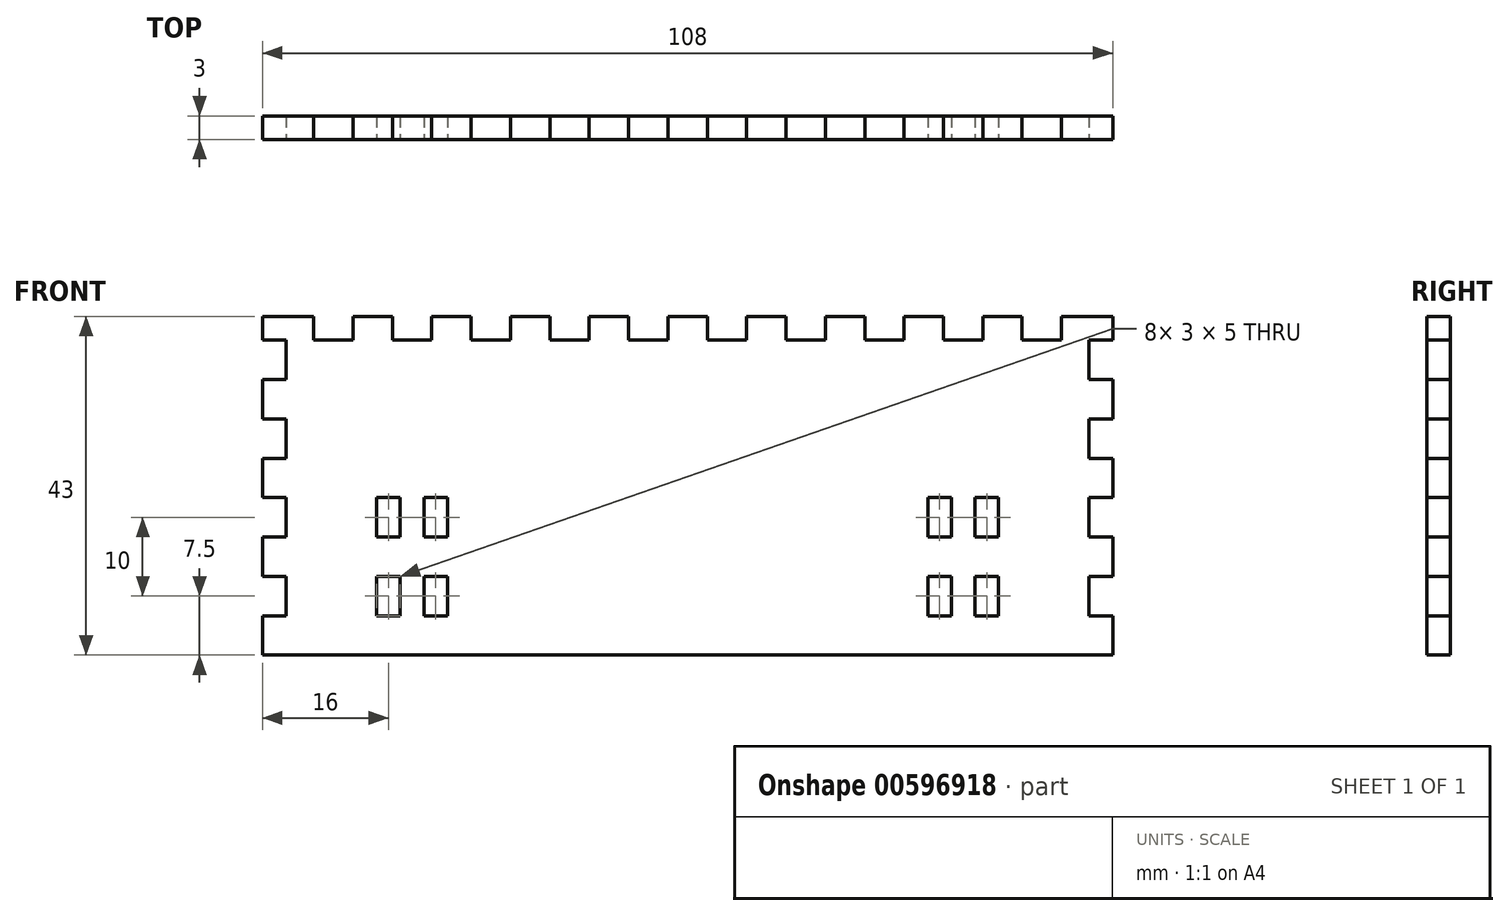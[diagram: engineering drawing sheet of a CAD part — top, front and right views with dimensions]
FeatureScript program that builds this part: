
annotation { "Feature Type Name" : "Feature", "Feature Type Description" : "" }
export const myFeature = defineFeature(function(context is Context, id is Id, definition is map)
    precondition{}
    {
        {
            var Q0;
            Q0=qCreatedBy(makeId("Front.planeOp"),FACE);
            var sketch = newSketch(context, id + "F0", { "sketchPlane" : qUnion([Q0])});
            skLineSegment(sketch, "E0.bottom", {"start": v(51, 20) * mm, "end": v(-51, 20) * mm});
            skLineSegment(sketch, "E0.top", {"start": v(51, -20) * mm, "end": v(-51, -20) * mm});
            skLineSegment(sketch, "E0.left", {"start": v(51, 20) * mm, "end": v(51, -20) * mm});
            skLineSegment(sketch, "E0.right", {"start": v(-51, 20) * mm, "end": v(-51, -20) * mm});
            skPoint(sketch, "E0.middle", {"position": v(0, 0) * mm});
            skSolve(sketch);
        }
        {
            var Q0;
            Q0=qSketchRegion(id+"F0",true);
            extrude(context, id + "F1", {"entities" : qUnion([Q0]), "depth" : 3 * mm, "offsetDistance" : 25 * mm});
        }
        {
            var Q0;
            Q0=makeQuery(id+"F1.opExtrude","CAP_FACE",FACE,{"disambiguationData":[OSD([sQuery(id+"F0.wireOp",EDGE,"E0.bottom"),sQuery(id+"F0.wireOp",EDGE,"E0.top"),sQuery(id+"F0.wireOp",EDGE,"E0.left"),sQuery(id+"F0.wireOp",EDGE,"E0.right")])],"isStart":false});
            var sketch = newSketch(context, id + "F2", { "sketchPlane" : qUnion([Q0])});
            skLineSegment(sketch, "E1.bottom", {"start": v(-51, -20) * mm, "end": v(-54, -20) * mm});
            skLineSegment(sketch, "E1.top", {"start": v(-51, -15) * mm, "end": v(-54, -15) * mm});
            skLineSegment(sketch, "E1.left", {"start": v(-51, -20) * mm, "end": v(-51, -15) * mm});
            skLineSegment(sketch, "E1.right", {"start": v(-54, -20) * mm, "end": v(-54, -15) * mm});
            skLineSegment(sketch, "E2.0.1.0", {"start": v(-51, -5) * mm, "end": v(-54, -5) * mm});
            skLineSegment(sketch, "E2.0.1.1", {"start": v(-54, -10) * mm, "end": v(-54, -5) * mm});
            skLineSegment(sketch, "E2.0.1.2", {"start": v(-51, -10) * mm, "end": v(-51, -5) * mm});
            skLineSegment(sketch, "E2.0.1.3", {"start": v(-51, -10) * mm, "end": v(-54, -10) * mm});
            skLineSegment(sketch, "E2.0.2.0", {"start": v(-51, 5) * mm, "end": v(-54, 5) * mm});
            skLineSegment(sketch, "E2.0.2.1", {"start": v(-54, 0) * mm, "end": v(-54, 5) * mm});
            skLineSegment(sketch, "E2.0.2.2", {"start": v(-51, 0) * mm, "end": v(-51, 5) * mm});
            skLineSegment(sketch, "E2.0.2.3", {"start": v(-51, 0) * mm, "end": v(-54, 0) * mm});
            skLineSegment(sketch, "E2.0.3.0", {"start": v(-51, 15) * mm, "end": v(-54, 15) * mm});
            skLineSegment(sketch, "E2.0.3.1", {"start": v(-54, 10) * mm, "end": v(-54, 15) * mm});
            skLineSegment(sketch, "E2.0.3.2", {"start": v(-51, 10) * mm, "end": v(-51, 15) * mm});
            skLineSegment(sketch, "E2.0.3.3", {"start": v(-51, 10) * mm, "end": v(-54, 10) * mm});
            skLineSegment(sketch, "E2.direction1", {"start": v(-54, -15) * mm, "end": v(-29, -15) * mm, "construction": true});
            skLineSegment(sketch, "E2.direction2", {"start": v(-54, -15) * mm, "end": v(-54, -5) * mm, "construction": true});
            skLineSegment(sketch, "E3.MirrorCS", {"start": v(54, -10) * mm, "end": v(54, -5) * mm});
            skLineSegment(sketch, "E4.MirrorCS", {"start": v(51, -5) * mm, "end": v(54, -5) * mm});
            skLineSegment(sketch, "E5.MirrorCS", {"start": v(51, -20) * mm, "end": v(51, -15) * mm});
            skLineSegment(sketch, "E6.MirrorCS", {"start": v(54, 10) * mm, "end": v(54, 15) * mm});
            skLineSegment(sketch, "E7.MirrorCS", {"start": v(51, -20) * mm, "end": v(54, -20) * mm});
            skLineSegment(sketch, "E8.MirrorCS", {"start": v(51, -15) * mm, "end": v(54, -15) * mm});
            skLineSegment(sketch, "E9.MirrorCS", {"start": v(54, -20) * mm, "end": v(54, -15) * mm});
            skLineSegment(sketch, "E10.MirrorCS", {"start": v(51, 15) * mm, "end": v(54, 15) * mm});
            skLineSegment(sketch, "E11.MirrorCS", {"start": v(51, 10) * mm, "end": v(54, 10) * mm});
            skLineSegment(sketch, "E12.MirrorCS", {"start": v(54, -15) * mm, "end": v(54, -5) * mm, "construction": true});
            skLineSegment(sketch, "E13.MirrorCS", {"start": v(51, 10) * mm, "end": v(51, 15) * mm});
            skLineSegment(sketch, "E14.MirrorCS", {"start": v(54, 0) * mm, "end": v(54, 5) * mm});
            skLineSegment(sketch, "E15.MirrorCS", {"start": v(51, 0) * mm, "end": v(51, 5) * mm});
            skLineSegment(sketch, "E16.MirrorCS", {"start": v(51, 0) * mm, "end": v(54, 0) * mm});
            skLineSegment(sketch, "E17.MirrorCS", {"start": v(51, -10) * mm, "end": v(51, -5) * mm});
            skLineSegment(sketch, "E18.MirrorCS", {"start": v(51, -10) * mm, "end": v(54, -10) * mm});
            skLineSegment(sketch, "E19.MirrorCS", {"start": v(51, 5) * mm, "end": v(54, 5) * mm});
            skSolve(sketch);
        }
        {
            var Q0;
            Q0=qSketchRegion(id+"F2",true);
            extrude(context, id + "F3", {"entities" : qUnion([Q0]), "operationType" : NewBodyOperationType.ADD, "oppositeDirection" : true, "depth" : 3 * mm, "offsetDistance" : 25 * mm});
        }
        {
            var Q0;
            Q0=makeQuery(id+"F3.boolean.opBoolean","MERGE",FACE,{"derivedFrom":[makeQuery(id+"F1.opExtrude","CAP_FACE",FACE,{"disambiguationData":[OSD([sQuery(id+"F0.wireOp",EDGE,"E0.bottom"),sQuery(id+"F0.wireOp",EDGE,"E0.top"),sQuery(id+"F0.wireOp",EDGE,"E0.left"),sQuery(id+"F0.wireOp",EDGE,"E0.right")])],"isStart":true}),makeQuery(id+"F3.opExtrude","CAP_FACE",FACE,{"disambiguationData":[OSD([sQuery(id+"F2.wireOp",EDGE,"E1.bottom"),sQuery(id+"F2.wireOp",EDGE,"E1.top"),sQuery(id+"F2.wireOp",EDGE,"E1.left"),sQuery(id+"F2.wireOp",EDGE,"E1.right")])],"isStart":false}),makeQuery(id+"F3.opExtrude","CAP_FACE",FACE,{"disambiguationData":[OSD([sQuery(id+"F2.wireOp",EDGE,"E2.0.1.0"),sQuery(id+"F2.wireOp",EDGE,"E2.0.1.1"),sQuery(id+"F2.wireOp",EDGE,"E2.0.1.2"),sQuery(id+"F2.wireOp",EDGE,"E2.0.1.3")])],"isStart":false}),makeQuery(id+"F3.opExtrude","CAP_FACE",FACE,{"disambiguationData":[OSD([sQuery(id+"F2.wireOp",EDGE,"E2.0.2.0"),sQuery(id+"F2.wireOp",EDGE,"E2.0.2.1"),sQuery(id+"F2.wireOp",EDGE,"E2.0.2.2"),sQuery(id+"F2.wireOp",EDGE,"E2.0.2.3")])],"isStart":false}),makeQuery(id+"F3.opExtrude","CAP_FACE",FACE,{"disambiguationData":[OSD([sQuery(id+"F2.wireOp",EDGE,"E2.0.3.0"),sQuery(id+"F2.wireOp",EDGE,"E2.0.3.1"),sQuery(id+"F2.wireOp",EDGE,"E2.0.3.2"),sQuery(id+"F2.wireOp",EDGE,"E2.0.3.3")])],"isStart":false}),makeQuery(id+"F3.opExtrude","CAP_FACE",FACE,{"disambiguationData":[OSD([sQuery(id+"F2.wireOp",EDGE,"E3.MirrorCS"),sQuery(id+"F2.wireOp",EDGE,"E4.MirrorCS"),sQuery(id+"F2.wireOp",EDGE,"E17.MirrorCS"),sQuery(id+"F2.wireOp",EDGE,"E18.MirrorCS")])],"isStart":false}),makeQuery(id+"F3.opExtrude","CAP_FACE",FACE,{"disambiguationData":[OSD([sQuery(id+"F2.wireOp",EDGE,"E5.MirrorCS"),sQuery(id+"F2.wireOp",EDGE,"E7.MirrorCS"),sQuery(id+"F2.wireOp",EDGE,"E8.MirrorCS"),sQuery(id+"F2.wireOp",EDGE,"E9.MirrorCS")])],"isStart":false}),makeQuery(id+"F3.opExtrude","CAP_FACE",FACE,{"disambiguationData":[OSD([sQuery(id+"F2.wireOp",EDGE,"E6.MirrorCS"),sQuery(id+"F2.wireOp",EDGE,"E10.MirrorCS"),sQuery(id+"F2.wireOp",EDGE,"E11.MirrorCS"),sQuery(id+"F2.wireOp",EDGE,"E13.MirrorCS")])],"isStart":false}),makeQuery(id+"F3.opExtrude","CAP_FACE",FACE,{"disambiguationData":[OSD([sQuery(id+"F2.wireOp",EDGE,"E14.MirrorCS"),sQuery(id+"F2.wireOp",EDGE,"E15.MirrorCS"),sQuery(id+"F2.wireOp",EDGE,"E16.MirrorCS"),sQuery(id+"F2.wireOp",EDGE,"E19.MirrorCS")])],"isStart":false})]});
            var sketch = newSketch(context, id + "F4", { "sketchPlane" : qUnion([Q0])});
            skLineSegment(sketch, "E20", {"start": v(0, 20) * mm, "end": v(0, 21.5) * mm, "construction": true});
            skLineSegment(sketch, "E21.bottom", {"start": v(-2.5, 20) * mm, "end": v(2.5, 20) * mm});
            skLineSegment(sketch, "E21.top", {"start": v(-2.5, 23) * mm, "end": v(2.5, 23) * mm});
            skLineSegment(sketch, "E21.left", {"start": v(-2.5, 20) * mm, "end": v(-2.5, 23) * mm});
            skLineSegment(sketch, "E21.right", {"start": v(2.5, 20) * mm, "end": v(2.5, 23) * mm});
            skPoint(sketch, "E21.middle", {"position": v(0, 21.5) * mm});
            skLineSegment(sketch, "E22.1.0.0", {"start": v(7.5, 23) * mm, "end": v(12.5, 23) * mm});
            skLineSegment(sketch, "E22.1.0.1", {"start": v(12.5, 20) * mm, "end": v(12.5, 23) * mm});
            skLineSegment(sketch, "E22.1.0.2", {"start": v(7.5, 20) * mm, "end": v(12.5, 20) * mm});
            skLineSegment(sketch, "E22.1.0.3", {"start": v(7.5, 20) * mm, "end": v(7.5, 23) * mm});
            skLineSegment(sketch, "E22.2.0.0", {"start": v(17.5, 23) * mm, "end": v(22.5, 23) * mm});
            skLineSegment(sketch, "E22.2.0.1", {"start": v(22.5, 20) * mm, "end": v(22.5, 23) * mm});
            skLineSegment(sketch, "E22.2.0.2", {"start": v(17.5, 20) * mm, "end": v(22.5, 20) * mm});
            skLineSegment(sketch, "E22.2.0.3", {"start": v(17.5, 20) * mm, "end": v(17.5, 23) * mm});
            skLineSegment(sketch, "E22.3.0.0", {"start": v(27.5, 23) * mm, "end": v(32.5, 23) * mm});
            skLineSegment(sketch, "E22.3.0.1", {"start": v(32.5, 20) * mm, "end": v(32.5, 23) * mm});
            skLineSegment(sketch, "E22.3.0.2", {"start": v(27.5, 20) * mm, "end": v(32.5, 20) * mm});
            skLineSegment(sketch, "E22.3.0.3", {"start": v(27.5, 20) * mm, "end": v(27.5, 23) * mm});
            skLineSegment(sketch, "E22.4.0.0", {"start": v(37.5, 23) * mm, "end": v(42.5, 23) * mm});
            skLineSegment(sketch, "E22.4.0.1", {"start": v(42.5, 20) * mm, "end": v(42.5, 23) * mm});
            skLineSegment(sketch, "E22.4.0.2", {"start": v(37.5, 20) * mm, "end": v(42.5, 20) * mm});
            skLineSegment(sketch, "E22.4.0.3", {"start": v(37.5, 20) * mm, "end": v(37.5, 23) * mm});
            skLineSegment(sketch, "E22.5.0.0", {"start": v(47.5, 23) * mm, "end": v(52.5, 23) * mm});
            skLineSegment(sketch, "E22.5.0.2", {"start": v(47.5, 20) * mm, "end": v(52.5, 20) * mm});
            skLineSegment(sketch, "E22.5.0.3", {"start": v(47.5, 20) * mm, "end": v(47.5, 23) * mm});
            skLineSegment(sketch, "E22.direction1", {"start": v(-2.5, 23) * mm, "end": v(7.5, 23) * mm, "construction": true});
            skLineSegment(sketch, "E23.MirrorCS", {"start": v(-47.5, 20) * mm, "end": v(-47.5, 23) * mm});
            skLineSegment(sketch, "E24.MirrorCS", {"start": v(-17.5, 20) * mm, "end": v(-17.5, 23) * mm});
            skLineSegment(sketch, "E25.MirrorCS", {"start": v(-22.5, 20) * mm, "end": v(-22.5, 23) * mm});
            skLineSegment(sketch, "E26.MirrorCS", {"start": v(-7.5, 20) * mm, "end": v(-7.5, 23) * mm});
            skLineSegment(sketch, "E27.MirrorCS", {"start": v(-12.5, 20) * mm, "end": v(-12.5, 23) * mm});
            skLineSegment(sketch, "E28.MirrorCS", {"start": v(-32.5, 20) * mm, "end": v(-32.5, 23) * mm});
            skLineSegment(sketch, "E29.MirrorCS", {"start": v(-37.5, 20) * mm, "end": v(-37.5, 23) * mm});
            skLineSegment(sketch, "E30.MirrorCS", {"start": v(-27.5, 20) * mm, "end": v(-27.5, 23) * mm});
            skLineSegment(sketch, "E31.MirrorCS", {"start": v(-42.5, 20) * mm, "end": v(-42.5, 23) * mm});
            skLineSegment(sketch, "E32.MirrorCS", {"start": v(-37.5, 23) * mm, "end": v(-42.5, 23) * mm});
            skLineSegment(sketch, "E33.MirrorCS", {"start": v(-47.5, 23) * mm, "end": v(-52.5, 23) * mm});
            skLineSegment(sketch, "E34.MirrorCS", {"start": v(-17.5, 20) * mm, "end": v(-22.5, 20) * mm});
            skLineSegment(sketch, "E35.MirrorCS", {"start": v(-17.5, 23) * mm, "end": v(-22.5, 23) * mm});
            skLineSegment(sketch, "E36.MirrorCS", {"start": v(-7.5, 20) * mm, "end": v(-12.5, 20) * mm});
            skLineSegment(sketch, "E37.MirrorCS", {"start": v(-7.5, 23) * mm, "end": v(-12.5, 23) * mm});
            skLineSegment(sketch, "E38.MirrorCS", {"start": v(-47.5, 20) * mm, "end": v(-52.5, 20) * mm});
            skLineSegment(sketch, "E39.MirrorCS", {"start": v(-27.5, 20) * mm, "end": v(-32.5, 20) * mm});
            skLineSegment(sketch, "E40.MirrorCS", {"start": v(-27.5, 23) * mm, "end": v(-32.5, 23) * mm});
            skLineSegment(sketch, "E41.MirrorCS", {"start": v(-37.5, 20) * mm, "end": v(-42.5, 20) * mm});
            skLineSegment(sketch, "E42", {"start": v(-52.5, 20) * mm, "end": v(-54, 20) * mm});
            skLineSegment(sketch, "E43", {"start": v(-54, 20) * mm, "end": v(-54, 23) * mm});
            skLineSegment(sketch, "E44", {"start": v(-54, 23) * mm, "end": v(-52.5, 23) * mm});
            skLineSegment(sketch, "E45.bottom", {"start": v(52.5, 23) * mm, "end": v(54, 23) * mm});
            skLineSegment(sketch, "E45.top", {"start": v(52.5, 20) * mm, "end": v(54, 20) * mm});
            skLineSegment(sketch, "E45.right", {"start": v(54, 23) * mm, "end": v(54, 20) * mm});
            skSolve(sketch);
        }
        {
            var Q0;
            Q0 = qSketchRegion(id + "F4", true);
            extrude(context, id + "F5", {"entities" : qUnion([Q0]), "operationType" : NewBodyOperationType.ADD, "oppositeDirection" : true, "depth" : 3 * mm, "offsetDistance" : 25 * mm});
        }
        {
            var Q0;
            Q0=makeQuery(id+"F5.boolean.opBoolean","MERGE",FACE,{"derivedFrom":[makeQuery(id+"F3.boolean.opBoolean","MERGE",FACE,{"derivedFrom":[makeQuery(id+"F1.opExtrude","CAP_FACE",FACE,{"disambiguationData":[OSD([sQuery(id+"F0.wireOp",EDGE,"E0.bottom"),sQuery(id+"F0.wireOp",EDGE,"E0.top"),sQuery(id+"F0.wireOp",EDGE,"E0.left"),sQuery(id+"F0.wireOp",EDGE,"E0.right")])],"isStart":false}),makeQuery(id+"F3.opExtrude","CAP_FACE",FACE,{"disambiguationData":[OSD([sQuery(id+"F2.wireOp",EDGE,"E1.bottom"),sQuery(id+"F2.wireOp",EDGE,"E1.top"),sQuery(id+"F2.wireOp",EDGE,"E1.left"),sQuery(id+"F2.wireOp",EDGE,"E1.right")])],"isStart":true}),makeQuery(id+"F3.opExtrude","CAP_FACE",FACE,{"disambiguationData":[OSD([sQuery(id+"F2.wireOp",EDGE,"E2.0.1.0"),sQuery(id+"F2.wireOp",EDGE,"E2.0.1.1"),sQuery(id+"F2.wireOp",EDGE,"E2.0.1.2"),sQuery(id+"F2.wireOp",EDGE,"E2.0.1.3")])],"isStart":true}),makeQuery(id+"F3.opExtrude","CAP_FACE",FACE,{"disambiguationData":[OSD([sQuery(id+"F2.wireOp",EDGE,"E2.0.2.0"),sQuery(id+"F2.wireOp",EDGE,"E2.0.2.1"),sQuery(id+"F2.wireOp",EDGE,"E2.0.2.2"),sQuery(id+"F2.wireOp",EDGE,"E2.0.2.3")])],"isStart":true}),makeQuery(id+"F3.opExtrude","CAP_FACE",FACE,{"disambiguationData":[OSD([sQuery(id+"F2.wireOp",EDGE,"E2.0.3.0"),sQuery(id+"F2.wireOp",EDGE,"E2.0.3.1"),sQuery(id+"F2.wireOp",EDGE,"E2.0.3.2"),sQuery(id+"F2.wireOp",EDGE,"E2.0.3.3")])],"isStart":true}),makeQuery(id+"F3.opExtrude","CAP_FACE",FACE,{"disambiguationData":[OSD([sQuery(id+"F2.wireOp",EDGE,"E3.MirrorCS"),sQuery(id+"F2.wireOp",EDGE,"E4.MirrorCS"),sQuery(id+"F2.wireOp",EDGE,"E17.MirrorCS"),sQuery(id+"F2.wireOp",EDGE,"E18.MirrorCS")])],"isStart":true}),makeQuery(id+"F3.opExtrude","CAP_FACE",FACE,{"disambiguationData":[OSD([sQuery(id+"F2.wireOp",EDGE,"E5.MirrorCS"),sQuery(id+"F2.wireOp",EDGE,"E7.MirrorCS"),sQuery(id+"F2.wireOp",EDGE,"E8.MirrorCS"),sQuery(id+"F2.wireOp",EDGE,"E9.MirrorCS")])],"isStart":true}),makeQuery(id+"F3.opExtrude","CAP_FACE",FACE,{"disambiguationData":[OSD([sQuery(id+"F2.wireOp",EDGE,"E6.MirrorCS"),sQuery(id+"F2.wireOp",EDGE,"E10.MirrorCS"),sQuery(id+"F2.wireOp",EDGE,"E11.MirrorCS"),sQuery(id+"F2.wireOp",EDGE,"E13.MirrorCS")])],"isStart":true}),makeQuery(id+"F3.opExtrude","CAP_FACE",FACE,{"disambiguationData":[OSD([sQuery(id+"F2.wireOp",EDGE,"E14.MirrorCS"),sQuery(id+"F2.wireOp",EDGE,"E15.MirrorCS"),sQuery(id+"F2.wireOp",EDGE,"E16.MirrorCS"),sQuery(id+"F2.wireOp",EDGE,"E19.MirrorCS")])],"isStart":true})]}),makeQuery(id+"F5.opExtrude","CAP_FACE",FACE,{"disambiguationData":[OSD([sQuery(id+"F4.wireOp",EDGE,"E21.bottom"),sQuery(id+"F4.wireOp",EDGE,"E21.top"),sQuery(id+"F4.wireOp",EDGE,"E21.left"),sQuery(id+"F4.wireOp",EDGE,"E21.right")])],"isStart":false}),makeQuery(id+"F5.opExtrude","CAP_FACE",FACE,{"disambiguationData":[OSD([sQuery(id+"F4.wireOp",EDGE,"E22.1.0.0"),sQuery(id+"F4.wireOp",EDGE,"E22.1.0.1"),sQuery(id+"F4.wireOp",EDGE,"E22.1.0.2"),sQuery(id+"F4.wireOp",EDGE,"E22.1.0.3")])],"isStart":false}),makeQuery(id+"F5.opExtrude","CAP_FACE",FACE,{"disambiguationData":[OSD([sQuery(id+"F4.wireOp",EDGE,"E22.2.0.0"),sQuery(id+"F4.wireOp",EDGE,"E22.2.0.1"),sQuery(id+"F4.wireOp",EDGE,"E22.2.0.2"),sQuery(id+"F4.wireOp",EDGE,"E22.2.0.3")])],"isStart":false}),makeQuery(id+"F5.opExtrude","CAP_FACE",FACE,{"disambiguationData":[OSD([sQuery(id+"F4.wireOp",EDGE,"E22.3.0.0"),sQuery(id+"F4.wireOp",EDGE,"E22.3.0.1"),sQuery(id+"F4.wireOp",EDGE,"E22.3.0.2"),sQuery(id+"F4.wireOp",EDGE,"E22.3.0.3")])],"isStart":false}),makeQuery(id+"F5.opExtrude","CAP_FACE",FACE,{"disambiguationData":[OSD([sQuery(id+"F4.wireOp",EDGE,"E22.4.0.0"),sQuery(id+"F4.wireOp",EDGE,"E22.4.0.1"),sQuery(id+"F4.wireOp",EDGE,"E22.4.0.2"),sQuery(id+"F4.wireOp",EDGE,"E22.4.0.3")])],"isStart":false}),makeQuery(id+"F5.opExtrude","CAP_FACE",FACE,{"disambiguationData":[OSD([sQuery(id+"F4.wireOp",EDGE,"E22.5.0.0"),sQuery(id+"F4.wireOp",EDGE,"E22.5.0.2"),sQuery(id+"F4.wireOp",EDGE,"E22.5.0.3"),sQuery(id+"F4.wireOp",EDGE,"E45.bottom"),sQuery(id+"F4.wireOp",EDGE,"E45.top"),sQuery(id+"F4.wireOp",EDGE,"E45.right")])],"isStart":false}),makeQuery(id+"F5.opExtrude","CAP_FACE",FACE,{"disambiguationData":[OSD([sQuery(id+"F4.wireOp",EDGE,"E23.MirrorCS"),sQuery(id+"F4.wireOp",EDGE,"E33.MirrorCS"),sQuery(id+"F4.wireOp",EDGE,"E38.MirrorCS"),sQuery(id+"F4.wireOp",EDGE,"E42"),sQuery(id+"F4.wireOp",EDGE,"E43"),sQuery(id+"F4.wireOp",EDGE,"E44")])],"isStart":false}),makeQuery(id+"F5.opExtrude","CAP_FACE",FACE,{"disambiguationData":[OSD([sQuery(id+"F4.wireOp",EDGE,"E24.MirrorCS"),sQuery(id+"F4.wireOp",EDGE,"E25.MirrorCS"),sQuery(id+"F4.wireOp",EDGE,"E34.MirrorCS"),sQuery(id+"F4.wireOp",EDGE,"E35.MirrorCS")])],"isStart":false}),makeQuery(id+"F5.opExtrude","CAP_FACE",FACE,{"disambiguationData":[OSD([sQuery(id+"F4.wireOp",EDGE,"E26.MirrorCS"),sQuery(id+"F4.wireOp",EDGE,"E27.MirrorCS"),sQuery(id+"F4.wireOp",EDGE,"E36.MirrorCS"),sQuery(id+"F4.wireOp",EDGE,"E37.MirrorCS")])],"isStart":false}),makeQuery(id+"F5.opExtrude","CAP_FACE",FACE,{"disambiguationData":[OSD([sQuery(id+"F4.wireOp",EDGE,"E28.MirrorCS"),sQuery(id+"F4.wireOp",EDGE,"E30.MirrorCS"),sQuery(id+"F4.wireOp",EDGE,"E39.MirrorCS"),sQuery(id+"F4.wireOp",EDGE,"E40.MirrorCS")])],"isStart":false}),makeQuery(id+"F5.opExtrude","CAP_FACE",FACE,{"disambiguationData":[OSD([sQuery(id+"F4.wireOp",EDGE,"E29.MirrorCS"),sQuery(id+"F4.wireOp",EDGE,"E31.MirrorCS"),sQuery(id+"F4.wireOp",EDGE,"E32.MirrorCS"),sQuery(id+"F4.wireOp",EDGE,"E41.MirrorCS")])],"isStart":false})]});
            var sketch = newSketch(context, id + "F6", { "sketchPlane" : qUnion([Q0])});
            skLineSegment(sketch, "E46", {"start": v(0, -20) * mm, "end": v(-32, -20) * mm, "construction": true});
            skLineSegment(sketch, "E47", {"start": v(-32, -20) * mm, "end": v(-32, -12.5) * mm, "construction": true});
            skLineSegment(sketch, "E48.bottom", {"start": v(-30.5, -10) * mm, "end": v(-33.5, -10) * mm});
            skLineSegment(sketch, "E48.top", {"start": v(-30.5, -15) * mm, "end": v(-33.5, -15) * mm});
            skLineSegment(sketch, "E48.left", {"start": v(-30.5, -10) * mm, "end": v(-30.5, -15) * mm});
            skLineSegment(sketch, "E48.right", {"start": v(-33.5, -10) * mm, "end": v(-33.5, -15) * mm});
            skPoint(sketch, "E48.middle", {"position": v(-32, -12.5) * mm});
            skLineSegment(sketch, "E49.0.1.0", {"start": v(-30.5, -5) * mm, "end": v(-33.5, -5) * mm});
            skLineSegment(sketch, "E49.0.1.1", {"start": v(-33.5, 0) * mm, "end": v(-33.5, -5) * mm});
            skLineSegment(sketch, "E49.0.1.2", {"start": v(-30.5, 0) * mm, "end": v(-33.5, 0) * mm});
            skLineSegment(sketch, "E49.0.1.3", {"start": v(-30.5, 0) * mm, "end": v(-30.5, -5) * mm});
            skLineSegment(sketch, "E49.0.1.4", {"start": v(0, -10) * mm, "end": v(-32, -10) * mm, "construction": true});
            skLineSegment(sketch, "E49.direction1", {"start": v(-33.5, -15) * mm, "end": v(-8.5, -15) * mm, "construction": true});
            skLineSegment(sketch, "E49.direction2", {"start": v(-33.5, -15) * mm, "end": v(-33.5, -5) * mm, "construction": true});
            skLineSegment(sketch, "E50", {"start": v(-32, -20) * mm, "end": v(-35, -20) * mm});
            skLineSegment(sketch, "E51", {"start": v(-35, -20) * mm, "end": v(-35, -15.8) * mm});
            skLineSegment(sketch, "E52.MirrorCS", {"start": v(-36.5, -10) * mm, "end": v(-36.5, -15) * mm});
            skLineSegment(sketch, "E53.MirrorCS", {"start": v(-36.5, -15) * mm, "end": v(-36.5, -5) * mm, "construction": true});
            skLineSegment(sketch, "E54.MirrorCS", {"start": v(-39.5, 0) * mm, "end": v(-39.5, -5) * mm});
            skLineSegment(sketch, "E55.MirrorCS", {"start": v(-39.5, -10) * mm, "end": v(-36.5, -10) * mm});
            skLineSegment(sketch, "E56.MirrorCS", {"start": v(-39.5, -15) * mm, "end": v(-36.5, -15) * mm});
            skLineSegment(sketch, "E57.MirrorCS", {"start": v(-39.5, -10) * mm, "end": v(-39.5, -15) * mm});
            skLineSegment(sketch, "E58.MirrorCS", {"start": v(-39.5, -5) * mm, "end": v(-36.5, -5) * mm});
            skLineSegment(sketch, "E59.MirrorCS", {"start": v(-36.5, 0) * mm, "end": v(-36.5, -5) * mm});
            skPoint(sketch, "E60.MirrorP", {"position": v(-38, -12.5) * mm});
            skLineSegment(sketch, "E61.MirrorCS", {"start": v(-39.5, 0) * mm, "end": v(-36.5, 0) * mm});
            skLineSegment(sketch, "E62.MirrorCS", {"start": v(30.5, -10) * mm, "end": v(33.5, -10) * mm});
            skLineSegment(sketch, "E63.MirrorCS", {"start": v(30.5, -15) * mm, "end": v(33.5, -15) * mm});
            skLineSegment(sketch, "E64.MirrorCS", {"start": v(30.5, -5) * mm, "end": v(33.5, -5) * mm});
            skLineSegment(sketch, "E65.MirrorCS", {"start": v(39.5, -10) * mm, "end": v(36.5, -10) * mm});
            skLineSegment(sketch, "E66.MirrorCS", {"start": v(39.5, 0) * mm, "end": v(36.5, 0) * mm});
            skLineSegment(sketch, "E67.MirrorCS", {"start": v(39.5, -15) * mm, "end": v(36.5, -15) * mm});
            skLineSegment(sketch, "E68.MirrorCS", {"start": v(39.5, -5) * mm, "end": v(36.5, -5) * mm});
            skLineSegment(sketch, "E69.MirrorCS", {"start": v(30.5, 0) * mm, "end": v(33.5, 0) * mm});
            skLineSegment(sketch, "E70.MirrorCS", {"start": v(39.5, -10) * mm, "end": v(39.5, -15) * mm});
            skLineSegment(sketch, "E71.MirrorCS", {"start": v(30.5, -10) * mm, "end": v(30.5, -15) * mm});
            skLineSegment(sketch, "E72.MirrorCS", {"start": v(33.5, -10) * mm, "end": v(33.5, -15) * mm});
            skLineSegment(sketch, "E73.MirrorCS", {"start": v(36.5, -10) * mm, "end": v(36.5, -15) * mm});
            skLineSegment(sketch, "E74.MirrorCS", {"start": v(33.5, 0) * mm, "end": v(33.5, -5) * mm});
            skPoint(sketch, "E75.MirrorP", {"position": v(32, -12.5) * mm});
            skLineSegment(sketch, "E76.MirrorCS", {"start": v(36.5, 0) * mm, "end": v(36.5, -5) * mm});
            skLineSegment(sketch, "E77.MirrorCS", {"start": v(33.5, -15) * mm, "end": v(33.5, -5) * mm, "construction": true});
            skLineSegment(sketch, "E78.MirrorCS", {"start": v(36.5, -15) * mm, "end": v(36.5, -5) * mm, "construction": true});
            skLineSegment(sketch, "E79.MirrorCS", {"start": v(30.5, 0) * mm, "end": v(30.5, -5) * mm});
            skPoint(sketch, "E80.MirrorP", {"position": v(38, -12.5) * mm});
            skLineSegment(sketch, "E81.MirrorCS", {"start": v(39.5, 0) * mm, "end": v(39.5, -5) * mm});
            skSolve(sketch);
        }
        {
            var Q0;
            Q0 = qSketchRegion(id + "F6", true);
            extrude(context, id + "F7", {"entities" : qUnion([Q0]), "operationType" : NewBodyOperationType.REMOVE, "oppositeDirection" : true, "depth" : 25 * mm, "offsetDistance" : 25 * mm});
        }
    });
